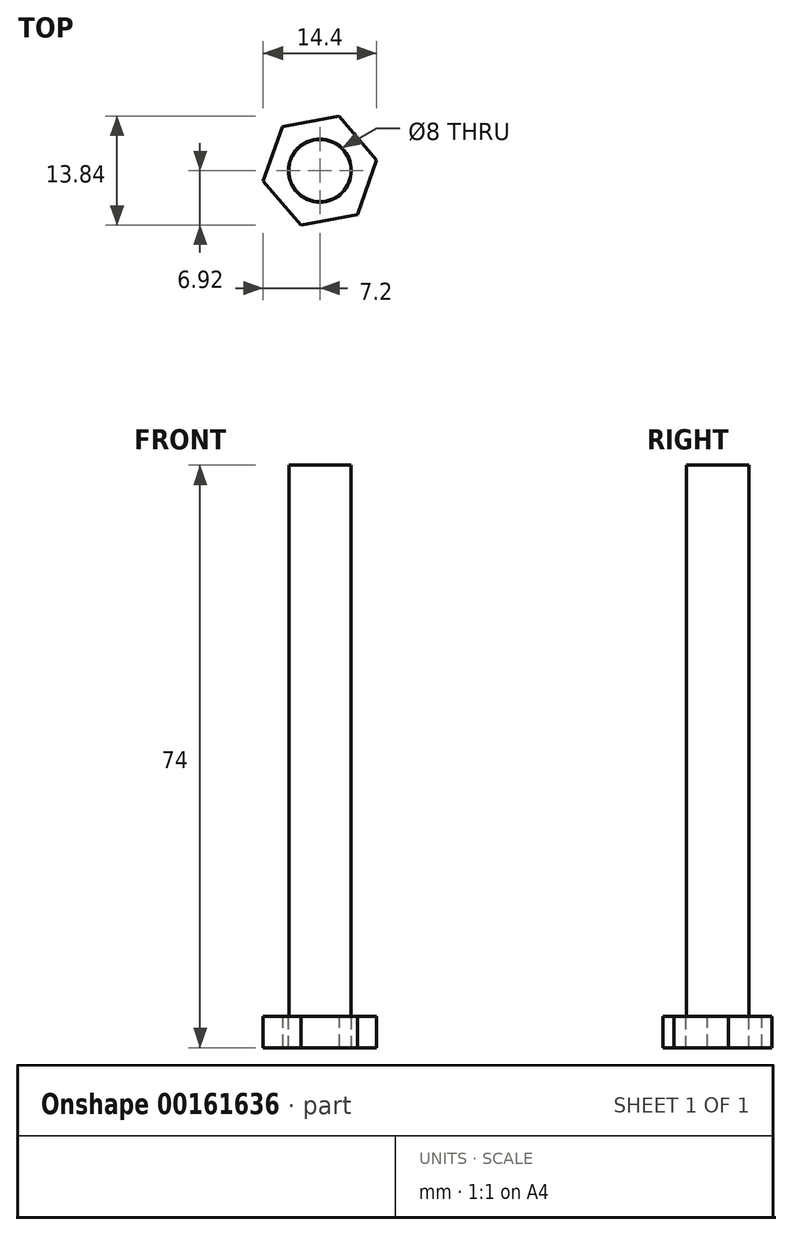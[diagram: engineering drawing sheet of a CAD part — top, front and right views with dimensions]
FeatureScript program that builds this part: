
annotation { "Feature Type Name" : "Feature", "Feature Type Description" : "" }
export const myFeature = defineFeature(function(context is Context, id is Id, definition is map)
    precondition{}
    {
        {
            var Q0;
            Q0=qCreatedBy(makeId("Top.planeOp"),FACE);
            var sketch = newSketch(context, id + "F0", { "sketchPlane" : qUnion([Q0])});
            skCircle(sketch, "E0.cCircle", {"center": v(0, 0) * mm, "radius": 6.35 * mm, "construction": true});
            skLineSegment(sketch, "E0.0", {"start": v(-4.78, 5.56) * mm, "end": v(2.43, 6.92) * mm});
            skLineSegment(sketch, "E0.1", {"start": v(2.43, 6.92) * mm, "end": v(7.2, 1.36) * mm});
            skLineSegment(sketch, "E0.2", {"start": v(7.2, 1.36) * mm, "end": v(4.78, -5.56) * mm});
            skLineSegment(sketch, "E0.3", {"start": v(4.78, -5.56) * mm, "end": v(-2.43, -6.92) * mm});
            skLineSegment(sketch, "E0.4", {"start": v(-2.43, -6.92) * mm, "end": v(-7.2, -1.36) * mm});
            skLineSegment(sketch, "E0.5", {"start": v(-7.2, -1.36) * mm, "end": v(-4.78, 5.56) * mm});
            skPoint(sketch, "E0.0.midPoint", {"position": v(-1.18, 6.24) * mm});
            skSolve(sketch);
        }
        {
            var Q0;
            Q0=qSketchRegion(id+"F0",true);
            extrude(context, id + "F1", {"entities" : qUnion([Q0]), "endBound" : BoundingType.SYMMETRIC, "depth" : 4 * mm});
        }
        {
            var Q0;
            Q0=makeQuery(id+"F1.opExtrude","CAP_FACE",FACE,{"disambiguationData":[OSD([sQuery(id+"F0.wireOp",EDGE,"E0.0"),sQuery(id+"F0.wireOp",EDGE,"E0.1"),sQuery(id+"F0.wireOp",EDGE,"E0.2"),sQuery(id+"F0.wireOp",EDGE,"E0.3"),sQuery(id+"F0.wireOp",EDGE,"E0.4"),sQuery(id+"F0.wireOp",EDGE,"E0.5")])],"isStart":false});
            var sketch = newSketch(context, id + "F2", { "sketchPlane" : qUnion([Q0])});
            skCircle(sketch, "E1", {"center": v(0, 0) * mm, "radius": 4 * mm});
            skSolve(sketch);
        }
        {
            var Q0;
            Q0=makeQuery(id+"F2.imprint","IMPRINT",FACE,{"disambiguationData":[TD([[makeQuery(id+"F2.imprint","IMPRINT",EDGE,{"derivedFrom":sQuery(id+"F2.wireOp",EDGE,"E1")}),1.0]])]});
            extrude(context, id + "F3", {"entities" : qUnion([Q0]), "operationType" : NewBodyOperationType.REMOVE, "oppositeDirection" : true, "depth" : 25 * mm});
        }
        {
            var Q0;
            Q0=makeQuery(id+"F1.opExtrude","CAP_FACE",FACE,{"disambiguationData":[OSD([sQuery(id+"F0.wireOp",EDGE,"E0.0"),sQuery(id+"F0.wireOp",EDGE,"E0.1"),sQuery(id+"F0.wireOp",EDGE,"E0.2"),sQuery(id+"F0.wireOp",EDGE,"E0.3"),sQuery(id+"F0.wireOp",EDGE,"E0.4"),sQuery(id+"F0.wireOp",EDGE,"E0.5")])],"isStart":false});
            var sketch = newSketch(context, id + "F4", { "sketchPlane" : qUnion([Q0])});
            skCircle(sketch, "E2", {"center": v(0, 0) * mm, "radius": 3.95 * mm});
            skSolve(sketch);
        }
        {
            var Q0;
            Q0=qSketchRegion(id+"F4",true);
            extrude(context, id + "F5", {"entities" : qUnion([Q0]), "operationType" : NewBodyOperationType.ADD, "depth" : 70 * mm});
        }
    });
